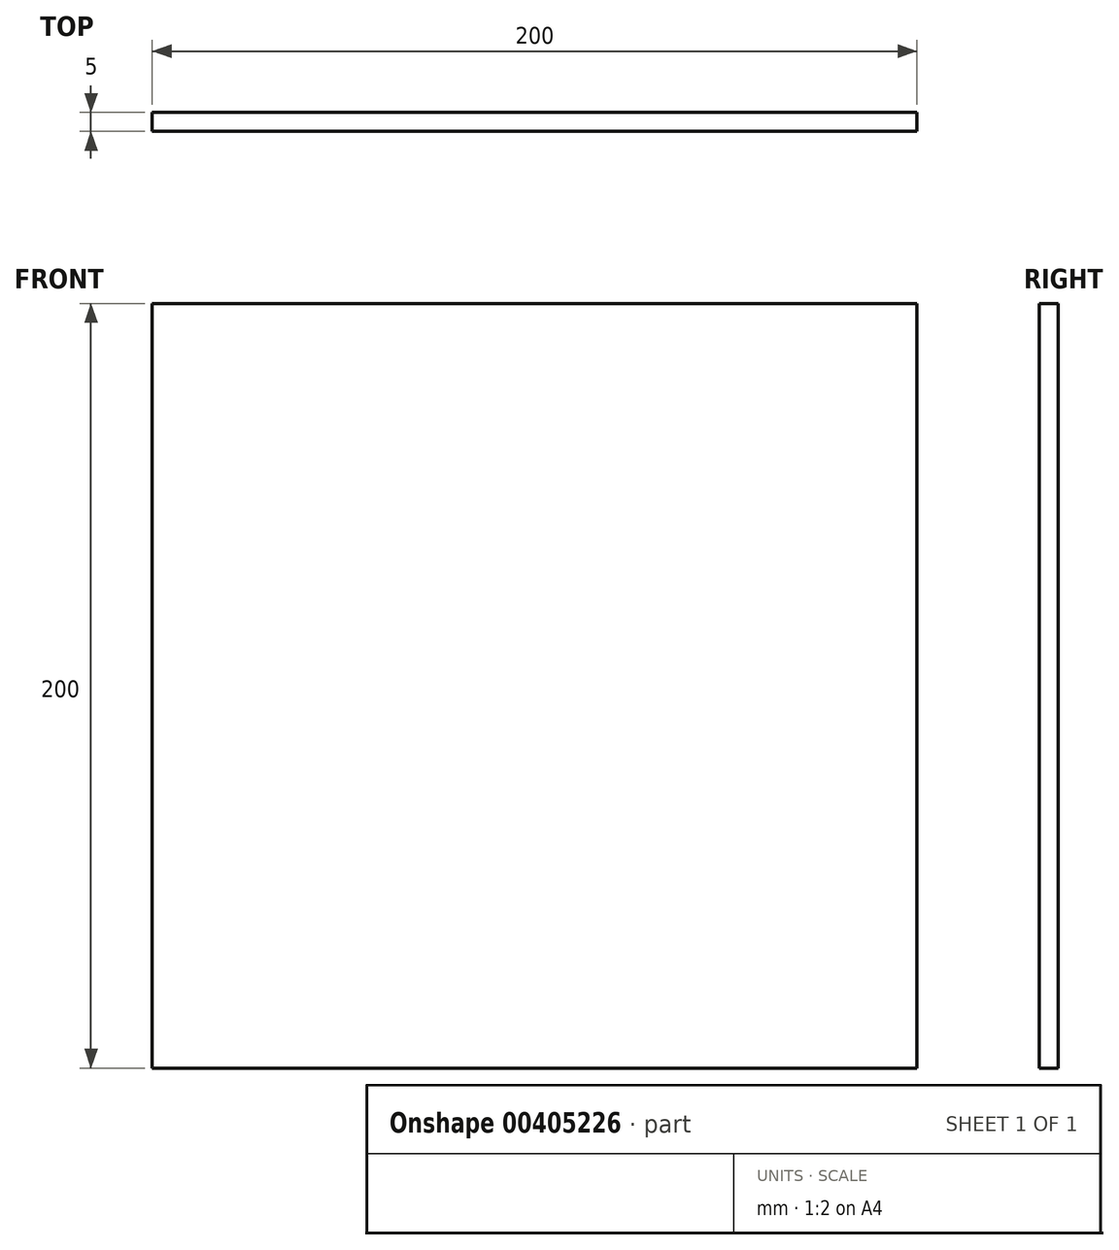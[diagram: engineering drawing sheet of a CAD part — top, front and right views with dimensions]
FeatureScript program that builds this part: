
annotation { "Feature Type Name" : "Feature", "Feature Type Description" : "" }
export const myFeature = defineFeature(function(context is Context, id is Id, definition is map)
    precondition{}
    {
        {
            var Q0;
            Q0=qCreatedBy(makeId("Front.planeOp"),FACE);
            var sketch = newSketch(context, id + "F0", { "sketchPlane" : qUnion([Q0])});
            skLineSegment(sketch, "E0.bottom", {"start": v(100, 100) * mm, "end": v(-100, 100) * mm});
            skLineSegment(sketch, "E0.top", {"start": v(100, -100) * mm, "end": v(-100, -100) * mm});
            skLineSegment(sketch, "E0.left", {"start": v(100, 100) * mm, "end": v(100, -100) * mm});
            skLineSegment(sketch, "E0.right", {"start": v(-100, 100) * mm, "end": v(-100, -100) * mm});
            skPoint(sketch, "E0.middle", {"position": v(0, 0) * mm});
            skSolve(sketch);
        }
        {
            var Q0;
            Q0 = qSketchRegion(id + "F0", true);
            extrude(context, id + "F1", {"entities" : qUnion([Q0]), "depth" : 5 * mm});
        }
    });
